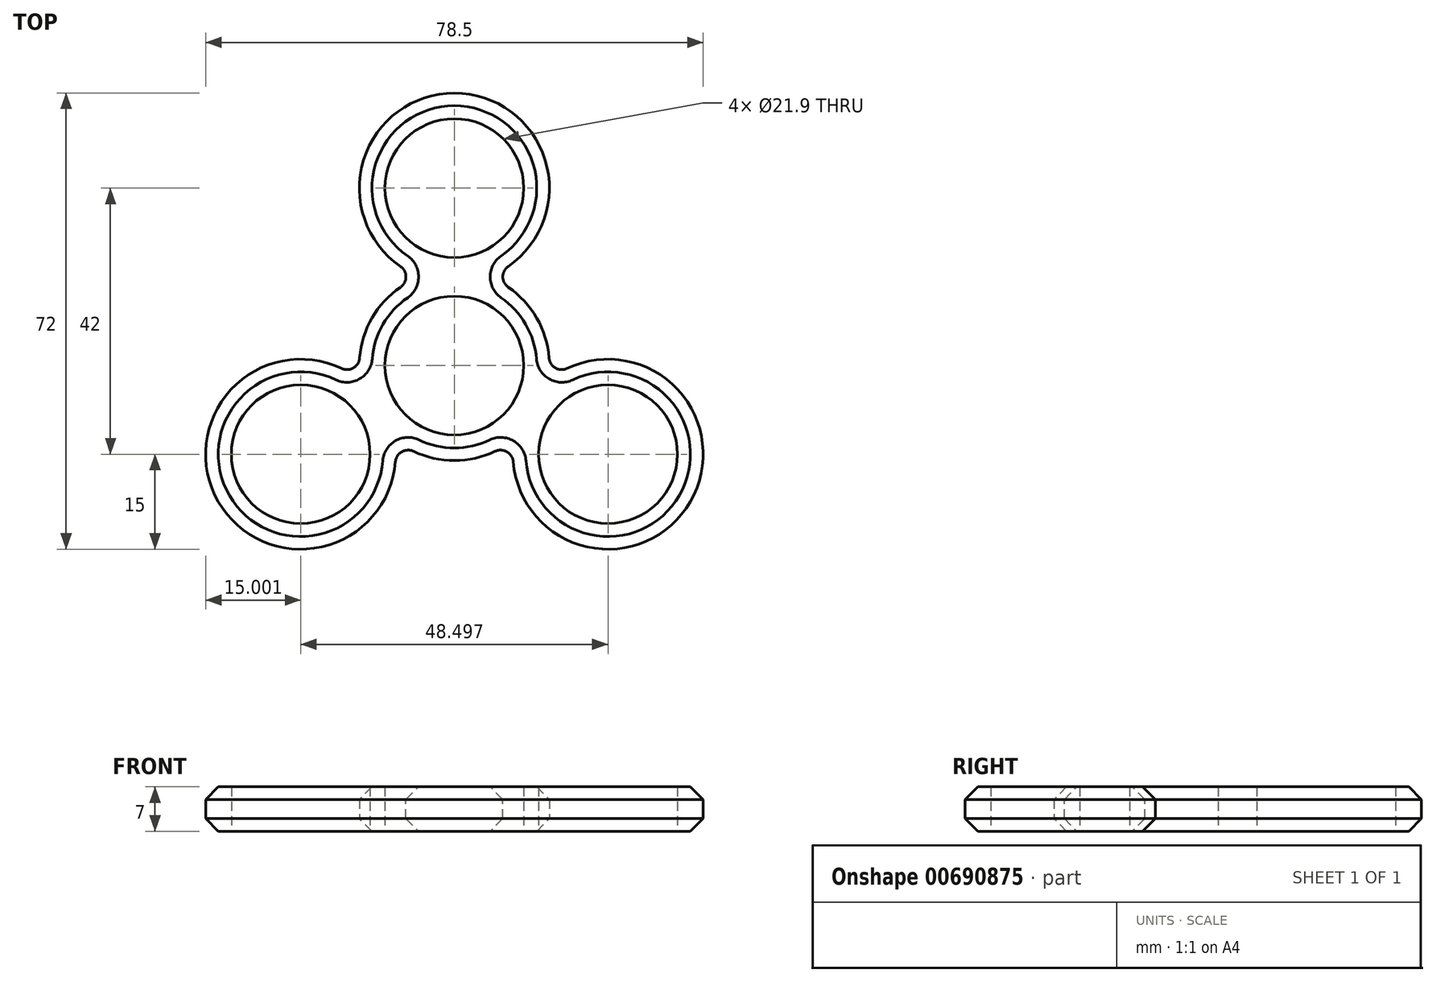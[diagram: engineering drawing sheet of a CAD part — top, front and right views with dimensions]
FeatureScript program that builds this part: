
annotation { "Feature Type Name" : "Feature", "Feature Type Description" : "" }
export const myFeature = defineFeature(function(context is Context, id is Id, definition is map)
    precondition{}
    {
        {
            var Q0;
            Q0=qCreatedBy(makeId("Top.planeOp"),FACE);
            var sketch = newSketch(context, id + "F0", { "sketchPlane" : qUnion([Q0])});
            skLineSegment(sketch, "E0", {"start": v(0, 0) * mm, "end": v(0, 28) * mm, "construction": true});
            skCircle(sketch, "E1", {"center": v(0, 28) * mm, "radius": 10.95 * mm});
            skArc(sketch, "E2", {"start": v(5.39, 14) * mm, "mid": v(0, 43) * mm, "end": v(-5.39, 14) * mm});
            skCircle(sketch, "E3", {"center": v(0, 0) * mm, "radius": 10.95 * mm});
            skArc(sketch, "E4", {"start": v(-9.43, -11.66) * mm, "mid": v(0, -15) * mm, "end": v(9.43, -11.66) * mm});
            skArc(sketch, "E5.1.2", {"start": v(-14.82, -2.34) * mm, "mid": v(-37.24, -21.5) * mm, "end": v(-9.43, -11.66) * mm});
            skCircle(sketch, "E5.1.3", {"center": v(-24.25, -14) * mm, "radius": 10.95 * mm});
            skArc(sketch, "E5.2.2", {"start": v(9.43, -11.66) * mm, "mid": v(37.24, -21.5) * mm, "end": v(14.82, -2.34) * mm});
            skCircle(sketch, "E5.2.3", {"center": v(24.25, -14) * mm, "radius": 10.95 * mm});
            skArc(sketch, "E6.trimOffspring", {"start": v(14.82, -2.34) * mm, "mid": v(13, 7.5) * mm, "end": v(5.39, 14) * mm});
            skArc(sketch, "E7.trimOffspring", {"start": v(-5.39, 14) * mm, "mid": v(-13, 7.5) * mm, "end": v(-14.82, -2.34) * mm});
            skLineSegment(sketch, "E8", {"start": v(0, 0) * mm, "end": v(-24.25, -14) * mm, "construction": true});
            skLineSegment(sketch, "E9", {"start": v(0, 0) * mm, "end": v(24.25, -14) * mm, "construction": true});
            skSolve(sketch);
        }
        {
            var Q0;
            Q0 = qSketchRegion(id + "F0", true);
            extrude(context, id + "F1", {"entities" : qUnion([Q0]), "depth" : 7 * mm, "offsetDistance" : 25 * mm});
        }
        {
            var Q0;
            Q0=makeQuery(id+"F1.opExtrude","SWEPT_EDGE",EDGE,{"disambiguationData":[OSD([sQuery(id+"F0.wireOp",EDGE,"E4"),sQuery(id+"F0.wireOp",EDGE,"E5.1.2")])]});
            var Q1;
            Q1=makeQuery(id+"F1.opExtrude","SWEPT_EDGE",EDGE,{"disambiguationData":[OSD([sQuery(id+"F0.wireOp",EDGE,"E4"),sQuery(id+"F0.wireOp",EDGE,"E5.2.2")])]});
            var Q2;
            Q2=makeQuery(id+"F1.opExtrude","SWEPT_EDGE",EDGE,{"disambiguationData":[OSD([sQuery(id+"F0.wireOp",EDGE,"E5.2.2"),sQuery(id+"F0.wireOp",EDGE,"E6.trimOffspring")])]});
            var Q3;
            Q3=makeQuery(id+"F1.opExtrude","SWEPT_EDGE",EDGE,{"disambiguationData":[OSD([sQuery(id+"F0.wireOp",EDGE,"E2"),sQuery(id+"F0.wireOp",EDGE,"E6.trimOffspring")])]});
            var Q4;
            Q4=makeQuery(id+"F1.opExtrude","SWEPT_EDGE",EDGE,{"disambiguationData":[OSD([sQuery(id+"F0.wireOp",EDGE,"E2"),sQuery(id+"F0.wireOp",EDGE,"E7.trimOffspring")])]});
            var Q5;
            Q5=makeQuery(id+"F1.opExtrude","SWEPT_EDGE",EDGE,{"disambiguationData":[OSD([sQuery(id+"F0.wireOp",EDGE,"E5.1.2"),sQuery(id+"F0.wireOp",EDGE,"E7.trimOffspring")])]});
            fillet(context, id + "F2", {"entities" : qUnion([Q0, Q1, Q2, Q3, Q4, Q5]), "radius" : 2 * mm, "tangentPropagation" : true, "allowEdgeOverflow" : false});
        }
        {
            var Q0;
            Q0=makeQuery(id+"F1.opExtrude","CAP_EDGE",EDGE,{"disambiguationData":[OSD([sQuery(id+"F0.wireOp",EDGE,"E5.2.2")])],"isStart":true});
            var Q1;
            Q1=makeQuery(id+"F1.opExtrude","CAP_EDGE",EDGE,{"disambiguationData":[OSD([sQuery(id+"F0.wireOp",EDGE,"E5.2.2")])],"isStart":false});
            chamfer(context, id + "F3", {"entities" : qUnion([Q0, Q1]), "width" : 2 * mm, "tangentPropagation" : true});
        }
    });
